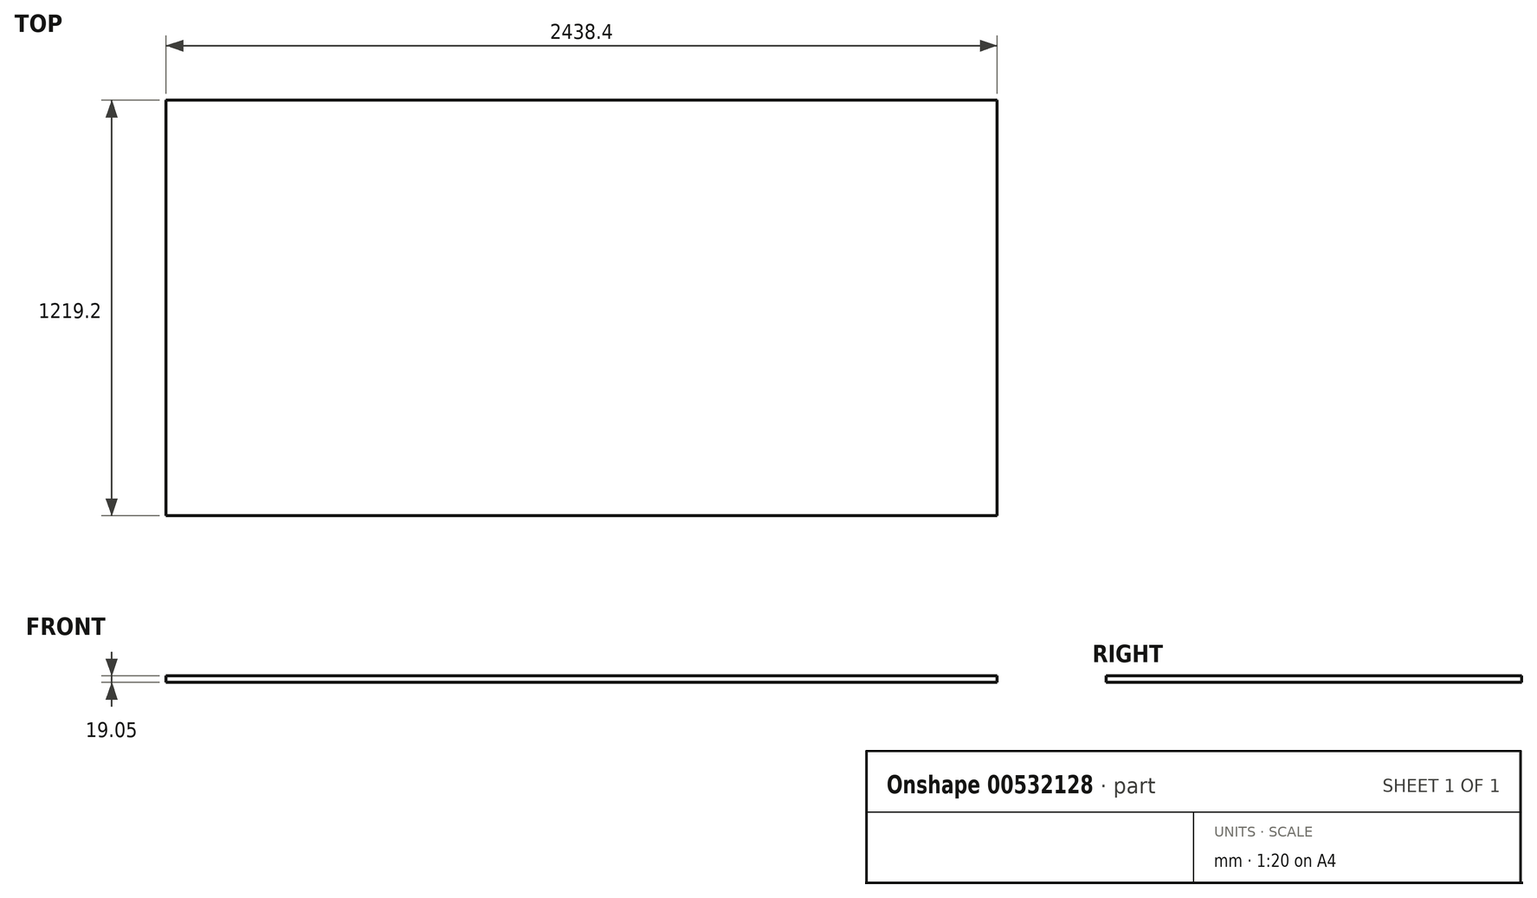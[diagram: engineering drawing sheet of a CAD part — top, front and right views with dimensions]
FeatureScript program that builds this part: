
annotation { "Feature Type Name" : "Feature", "Feature Type Description" : "" }
export const myFeature = defineFeature(function(context is Context, id is Id, definition is map)
    precondition{}
    {
        {
            var Q0;
            Q0=qCreatedBy(makeId("Top.planeOp"),FACE);
            var sketch = newSketch(context, id + "F0", { "sketchPlane" : qUnion([Q0])});
            skLineSegment(sketch, "E0.bottom", {"start": v(1219.2, -609.6) * mm, "end": v(-1219.2, -609.6) * mm});
            skLineSegment(sketch, "E0.top", {"start": v(1219.2, 609.6) * mm, "end": v(-1219.2, 609.6) * mm});
            skLineSegment(sketch, "E0.left", {"start": v(1219.2, -609.6) * mm, "end": v(1219.2, 609.6) * mm});
            skLineSegment(sketch, "E0.right", {"start": v(-1219.2, -609.6) * mm, "end": v(-1219.2, 609.6) * mm});
            skPoint(sketch, "E0.middle", {"position": v(0, 0) * mm});
            skSolve(sketch);
        }
        {
            var Q0;
            Q0 = qSketchRegion(id + "F0", true);
            extrude(context, id + "F1", {"entities" : qUnion([Q0]), "depth" : 19.05 * mm, "offsetDistance" : 25.4 * mm});
        }
    });
